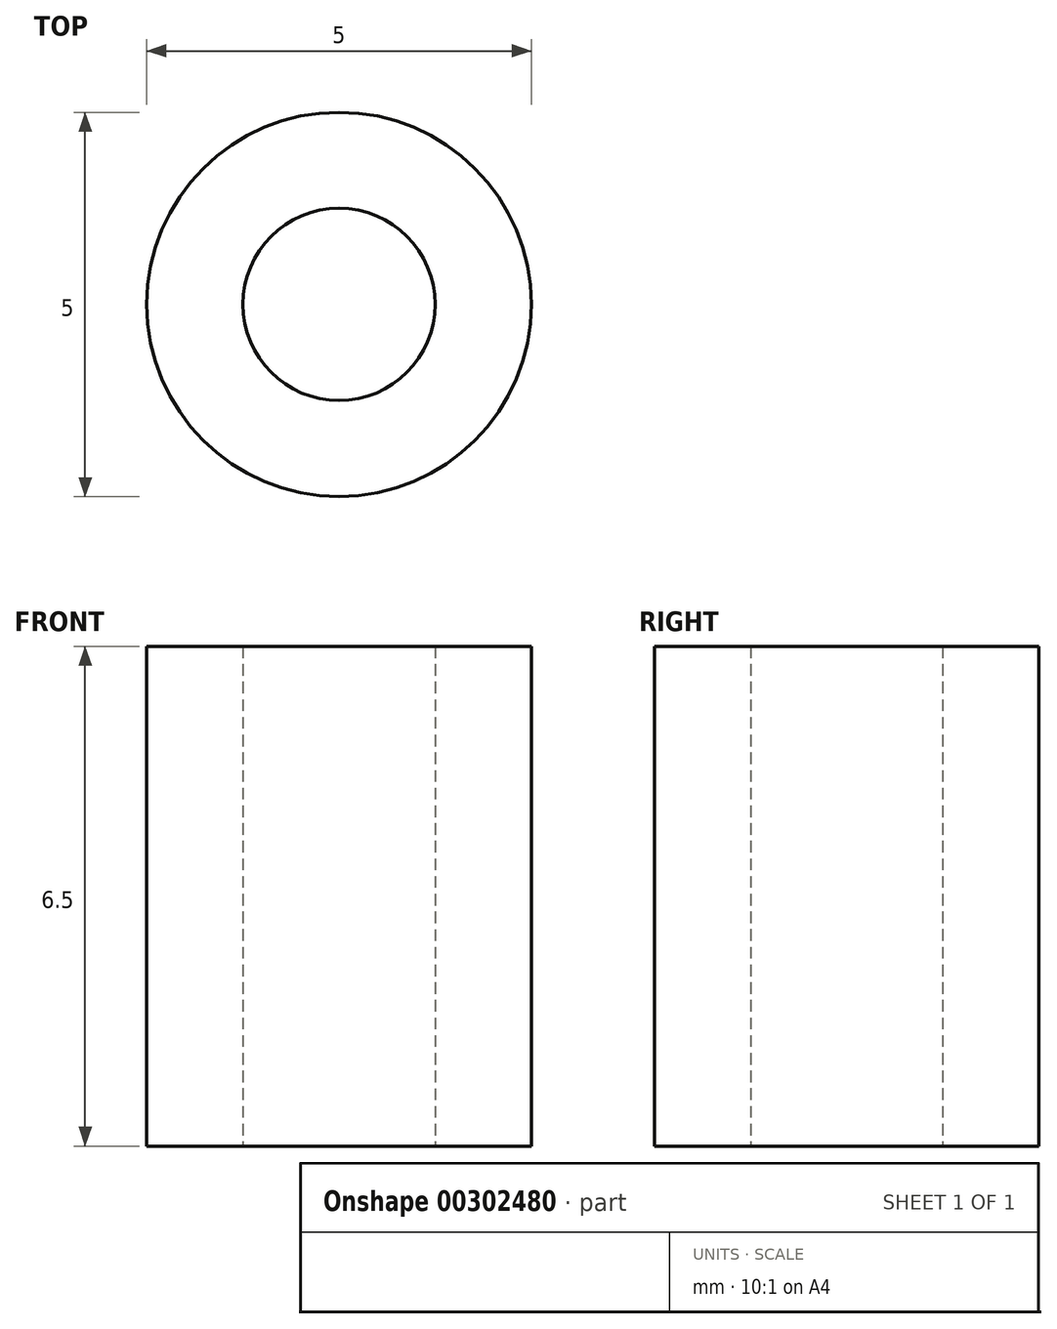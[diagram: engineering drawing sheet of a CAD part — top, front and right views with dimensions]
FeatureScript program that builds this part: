
annotation { "Feature Type Name" : "Feature", "Feature Type Description" : "" }
export const myFeature = defineFeature(function(context is Context, id is Id, definition is map)
    precondition{}
    {
        {
            var Q0;
            Q0=qCreatedBy(makeId("Top.planeOp"),FACE);
            var sketch = newSketch(context, id + "F0", { "sketchPlane" : qUnion([Q0])});
            skCircle(sketch, "E0", {"center": v(0, 0) * mm, "radius": 1.25 * mm});
            skCircle(sketch, "E1", {"center": v(0, 0) * mm, "radius": 2.5 * mm});
            skSolve(sketch);
        }
        {
            var Q0;
            Q0=makeQuery(id+"F0.imprint","IMPRINT",FACE,{"disambiguationData":[TD([[makeQuery(id+"F0.imprint","IMPRINT",EDGE,{"derivedFrom":sQuery(id+"F0.wireOp",EDGE,"E0")}),-1.0]])]});
            extrude(context, id + "F1", {"entities" : qUnion([Q0]), "depth" : 6.5 * mm});
        }
    });
